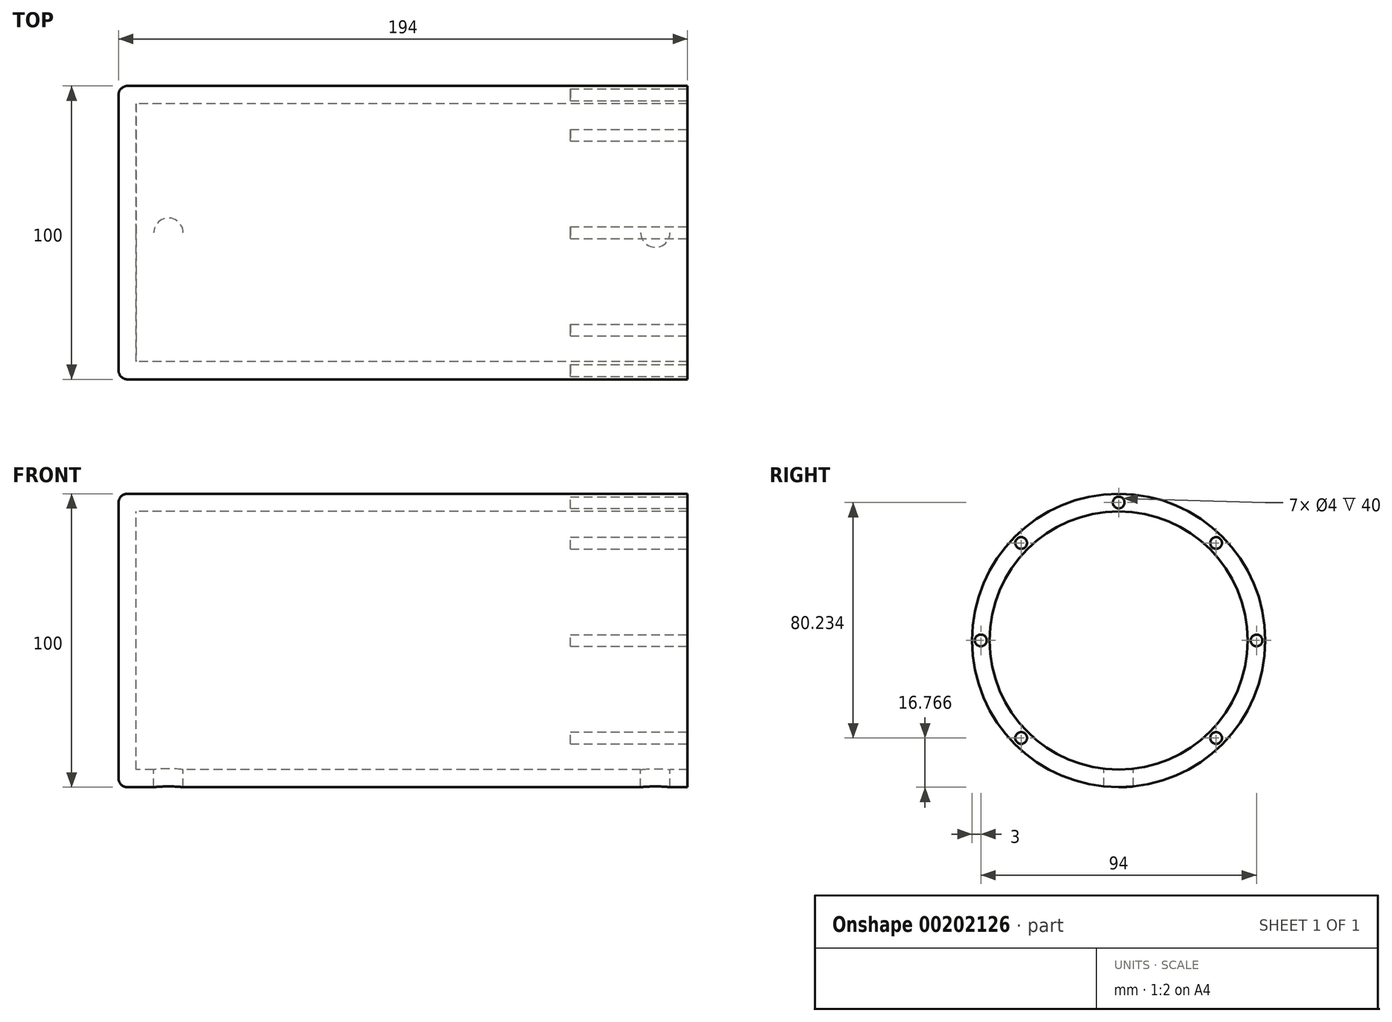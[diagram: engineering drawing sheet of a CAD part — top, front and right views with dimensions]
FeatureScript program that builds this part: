
annotation { "Feature Type Name" : "Feature", "Feature Type Description" : "" }
export const myFeature = defineFeature(function(context is Context, id is Id, definition is map)
    precondition{}
    {
        {
            var Q0;
            Q0=qCreatedBy(makeId("Right.planeOp"),FACE);
            var sketch = newSketch(context, id + "F0", { "sketchPlane" : qUnion([Q0])});
            skCircle(sketch, "E0", {"center": v(0, 0) * mm, "radius": 50 * mm});
            skSolve(sketch);
        }
        {
            var Q0;
            Q0=makeQuery(id+"F0.imprint","IMPRINT",FACE,{"disambiguationData":[TD([[makeQuery(id+"F0.imprint","IMPRINT",EDGE,{"derivedFrom":sQuery(id+"F0.wireOp",EDGE,"E0")}),1.0]])]});
            extrude(context, id + "F1", {"entities" : qUnion([Q0]), "endBound" : BoundingType.SYMMETRIC, "depth" : 194 * mm});
        }
        {
            var Q0;
            Q0=makeQuery(id+"F1.opExtrude","CAP_FACE",FACE,{"disambiguationData":[OSD([sQuery(id+"F0.wireOp",EDGE,"E0")])],"isStart":false});
            shell(context, id + "F2", {"entities" : qUnion([Q0]), "thickness" : 6 * mm});
        }
        {
            var Q0;
            Q0=makeQuery(id+"F1.opExtrude","CAP_FACE",FACE,{"disambiguationData":[OSD([sQuery(id+"F0.wireOp",EDGE,"E0")])],"isStart":false});
            var sketch = newSketch(context, id + "F3", { "sketchPlane" : qUnion([Q0])});
            skCircle(sketch, "E1", {"center": v(-47, 0) * mm, "radius": 2 * mm});
            skCircle(sketch, "E2.1.0", {"center": v(-33.23, 33.23) * mm, "radius": 2 * mm});
            skCircle(sketch, "E2.2.0", {"center": v(0, 47) * mm, "radius": 2 * mm});
            skPoint(sketch, "E2.center", {"position": v(0, 0) * mm});
            skLineSegment(sketch, "E2.anchor1", {"start": v(0, 0) * mm, "end": v(-47, 0) * mm, "construction": true});
            skLineSegment(sketch, "E2.anchor2", {"start": v(0, 0) * mm, "end": v(0, 47) * mm, "construction": true});
            skCircle(sketch, "E3.1.0", {"center": v(33.23, 33.23) * mm, "radius": 2 * mm});
            skCircle(sketch, "E3.2.0", {"center": v(47, 0) * mm, "radius": 2 * mm});
            skLineSegment(sketch, "E3.anchor2", {"start": v(0, 0) * mm, "end": v(47, 0) * mm, "construction": true});
            skCircle(sketch, "E4.MirrorC", {"center": v(-33.23, -33.23) * mm, "radius": 2 * mm});
            skCircle(sketch, "E5.MirrorC", {"center": v(33.23, -33.23) * mm, "radius": 2 * mm});
            skSolve(sketch);
        }
        {
            var Q0;
            Q0 = qSketchRegion(id + "F3", true);
            extrude(context, id + "F4", {"entities" : qUnion([Q0]), "operationType" : NewBodyOperationType.REMOVE, "oppositeDirection" : true, "depth" : 40 * mm});
        }
        {
            var Q0;
            Q0=makeQuery(id+"F1.opExtrude","CAP_EDGE",EDGE,{"disambiguationData":[OSD([sQuery(id+"F0.wireOp",EDGE,"E0")])],"isStart":true});
            fillet(context, id + "F5", {"entities" : qUnion([Q0]), "radius" : 3 * mm, "tangentPropagation" : true, "allowEdgeOverflow" : false});
        }
        {
            var Q0;
            Q0=qCreatedBy(makeId("Top.planeOp"),FACE);
            var sketch = newSketch(context, id + "F6", { "sketchPlane" : qUnion([Q0])});
            skCircle(sketch, "E6", {"center": v(-80, 0) * mm, "radius": 5 * mm});
            skCircle(sketch, "E7", {"center": v(86, 0) * mm, "radius": 5 * mm});
            skSolve(sketch);
        }
        {
            var Q0;
            Q0 = qSketchRegion(id + "F6", true);
            extrude(context, id + "F7", {"entities" : qUnion([Q0]), "operationType" : NewBodyOperationType.REMOVE, "endBound" : BoundingType.THROUGH_ALL, "oppositeDirection" : true, "depth" : 25 * mm});
        }
    });
